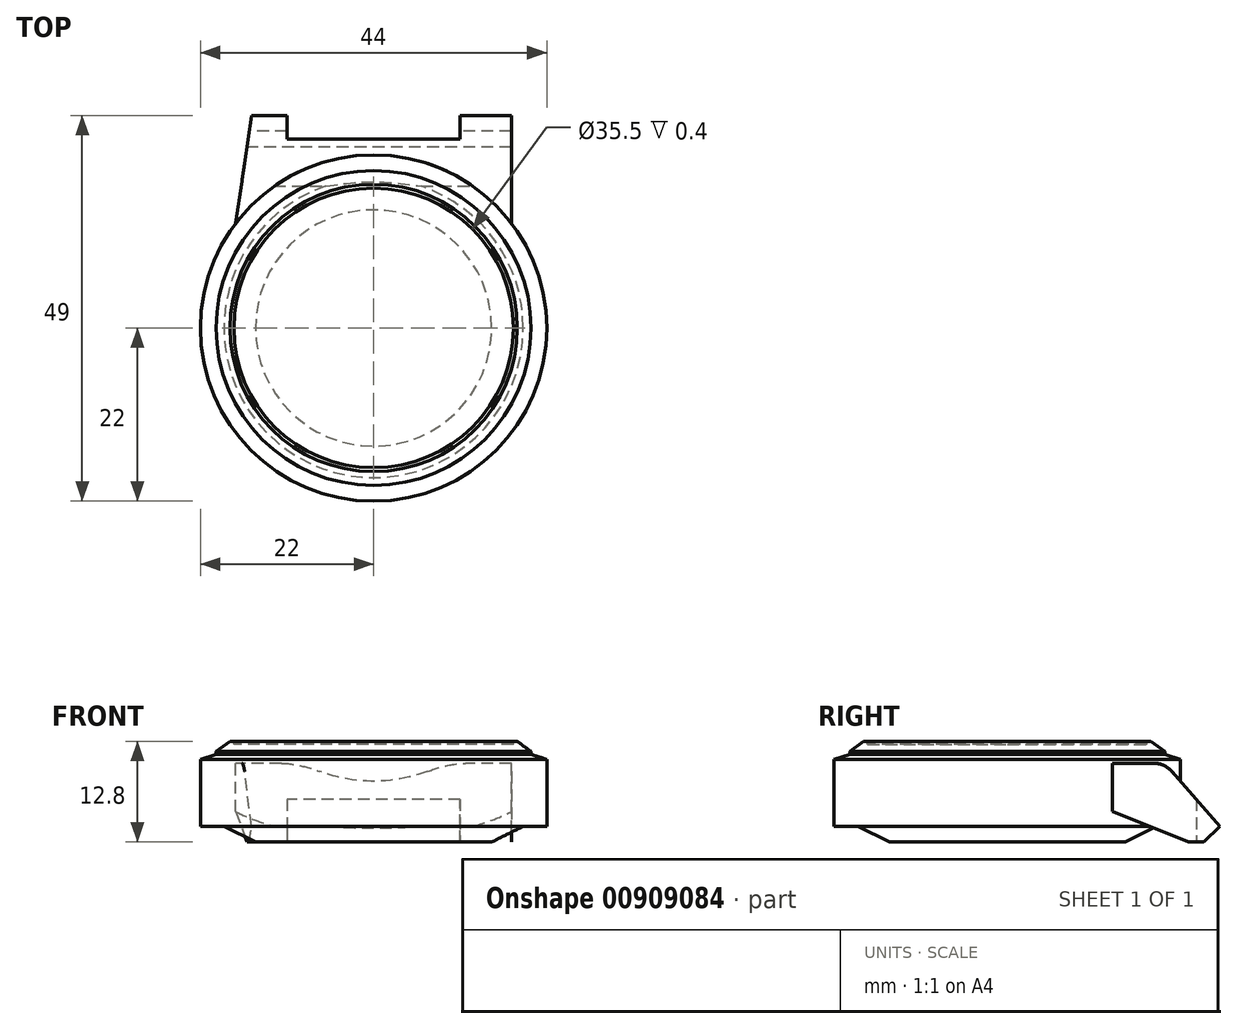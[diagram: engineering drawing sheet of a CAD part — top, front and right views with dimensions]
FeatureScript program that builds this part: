
annotation { "Feature Type Name" : "Feature", "Feature Type Description" : "" }
export const myFeature = defineFeature(function(context is Context, id is Id, definition is map)
    precondition{}
    {
        {
            var Q0;
            Q0=qCreatedBy(makeId("Front.planeOp"),FACE);
            var sketch = newSketch(context, id + "F0", { "sketchPlane" : qUnion([Q0])});
            skLineSegment(sketch, "E0", {"start": v(0, 0) * mm, "end": v(-15, 0) * mm});
            skLineSegment(sketch, "E1", {"start": v(-15, 0) * mm, "end": v(-19, 2) * mm});
            skLineSegment(sketch, "E2", {"start": v(-19, 2) * mm, "end": v(-22, 2) * mm});
            skLineSegment(sketch, "E3", {"start": v(-22, 2) * mm, "end": v(-22, 10.5) * mm});
            skLineSegment(sketch, "E4", {"start": v(-20, 11.5) * mm, "end": v(-18.25, 12.8) * mm});
            skLineSegment(sketch, "E5", {"start": v(-18.25, 12.8) * mm, "end": v(-17.75, 12.8) * mm});
            skLineSegment(sketch, "E6", {"start": v(-17.75, 12.8) * mm, "end": v(-17.75, 12.4) * mm});
            skLineSegment(sketch, "E7", {"start": v(-17.75, 12.4) * mm, "end": v(0, 12.4) * mm});
            skLineSegment(sketch, "E8", {"start": v(0, 12.4) * mm, "end": v(0, 0) * mm});
            skLineSegment(sketch, "E9", {"start": v(0, 23.3) * mm, "end": v(0, -16.5) * mm, "construction": true});
            skLineSegment(sketch, "E10", {"start": v(-22, 10.5) * mm, "end": v(-20, 11.14) * mm});
            skLineSegment(sketch, "E11", {"start": v(-20, 11.14) * mm, "end": v(-20, 11.5) * mm});
            skSolve(sketch);
        }
        {
            var Q0;
            Q0 = qSketchRegion(id + "F0", true);
            var Q1;
            Q1=sQuery(id+"F0.wireOp",EDGE,"E9");
            revolve(context, id + "F1", {"surfaceOperationType" : NewSurfaceOperationType.NEW, "entities" : qUnion([Q0]), "axis" : qUnion([Q1]), "revolveType" : RevolveType.FULL});
        }
        {
            var Q0;
            Q0=qCreatedBy(makeId("Right.planeOp"),FACE);
            var sketch = newSketch(context, id + "F2", { "sketchPlane" : qUnion([Q0])});
            skLineSegment(sketch, "E12", {"start": v(25, 0) * mm, "end": v(23, 0) * mm});
            skLineSegment(sketch, "E13", {"start": v(23, 0) * mm, "end": v(13, 4) * mm});
            skLineSegment(sketch, "E14", {"start": v(13, 10) * mm, "end": v(18.64, 10) * mm});
            skLineSegment(sketch, "E15", {"start": v(20.9, 8.98) * mm, "end": v(27, 2) * mm});
            skLineSegment(sketch, "E16", {"start": v(27, 2) * mm, "end": v(25, 0) * mm});
            skLineSegment(sketch, "E17", {"start": v(13, 10) * mm, "end": v(13, 4) * mm});
            skPoint(sketch, "E18.visualSharp", {"position": v(20, 10) * mm});
            skArc(sketch, "E18.filletArc", {"start": v(20.9, 8.98) * mm, "mid": v(19.88, 9.73) * mm, "end": v(18.64, 10) * mm});
            skSolve(sketch);
        }
        {
            var Q0;
            Q0 = qSketchRegion(id + "F2", true);
            extrude(context, id + "F3", {"entities" : qUnion([Q0]), "operationType" : NewBodyOperationType.ADD, "endBound" : BoundingType.SYMMETRIC, "depth" : 35 * mm, "offsetDistance" : 25 * mm});
        }
        {
            var Q0;
            Q0=qCreatedBy(makeId("Top.planeOp"),FACE);
            var sketch = newSketch(context, id + "F4", { "sketchPlane" : qUnion([Q0])});
            skLineSegment(sketch, "E19.0", {"start": v(-17.5, 13.33) * mm, "end": v(-17.5, 27) * mm});
            skLineSegment(sketch, "E20.0", {"start": v(-15.5, 27) * mm, "end": v(-17.5, 27) * mm});
            skLineSegment(sketch, "E21", {"start": v(-17.5, 13.33) * mm, "end": v(-15.5, 27) * mm});
            skPoint(sketch, "E22.orphan", {"position": v(-17.5, 18.64) * mm});
            skPoint(sketch, "E23.orphan", {"position": v(17.5, 27) * mm});
            skSolve(sketch);
        }
        {
            var Q0;
            Q0 = qSketchRegion(id + "F4", true);
            extrude(context, id + "F5", {"entities" : qUnion([Q0]), "operationType" : NewBodyOperationType.REMOVE, "endBound" : BoundingType.THROUGH_ALL, "depth" : 25 * mm, "offsetDistance" : 25 * mm});
        }
        {
            var Q0;
            Q0=qCreatedBy(makeId("Top.planeOp"),FACE);
            var sketch = newSketch(context, id + "F6", { "sketchPlane" : qUnion([Q0])});
            skLineSegment(sketch, "E24.0", {"start": v(11, 27) * mm, "end": v(-11, 27) * mm});
            skLineSegment(sketch, "E25", {"start": v(-11, 27) * mm, "end": v(-11, 24) * mm});
            skLineSegment(sketch, "E26", {"start": v(-11, 24) * mm, "end": v(11, 24) * mm});
            skLineSegment(sketch, "E27", {"start": v(11, 24) * mm, "end": v(11, 27) * mm});
            skPoint(sketch, "E28.orphan", {"position": v(15.5, 27) * mm});
            skPoint(sketch, "E29.orphan", {"position": v(-15.5, 27) * mm});
            skSolve(sketch);
        }
        {
            var Q0;
            Q0 = qSketchRegion(id + "F6", true);
            extrude(context, id + "F7", {"entities" : qUnion([Q0]), "operationType" : NewBodyOperationType.REMOVE, "endBound" : BoundingType.THROUGH_ALL, "depth" : 25 * mm, "offsetDistance" : 25 * mm});
        }
    });
